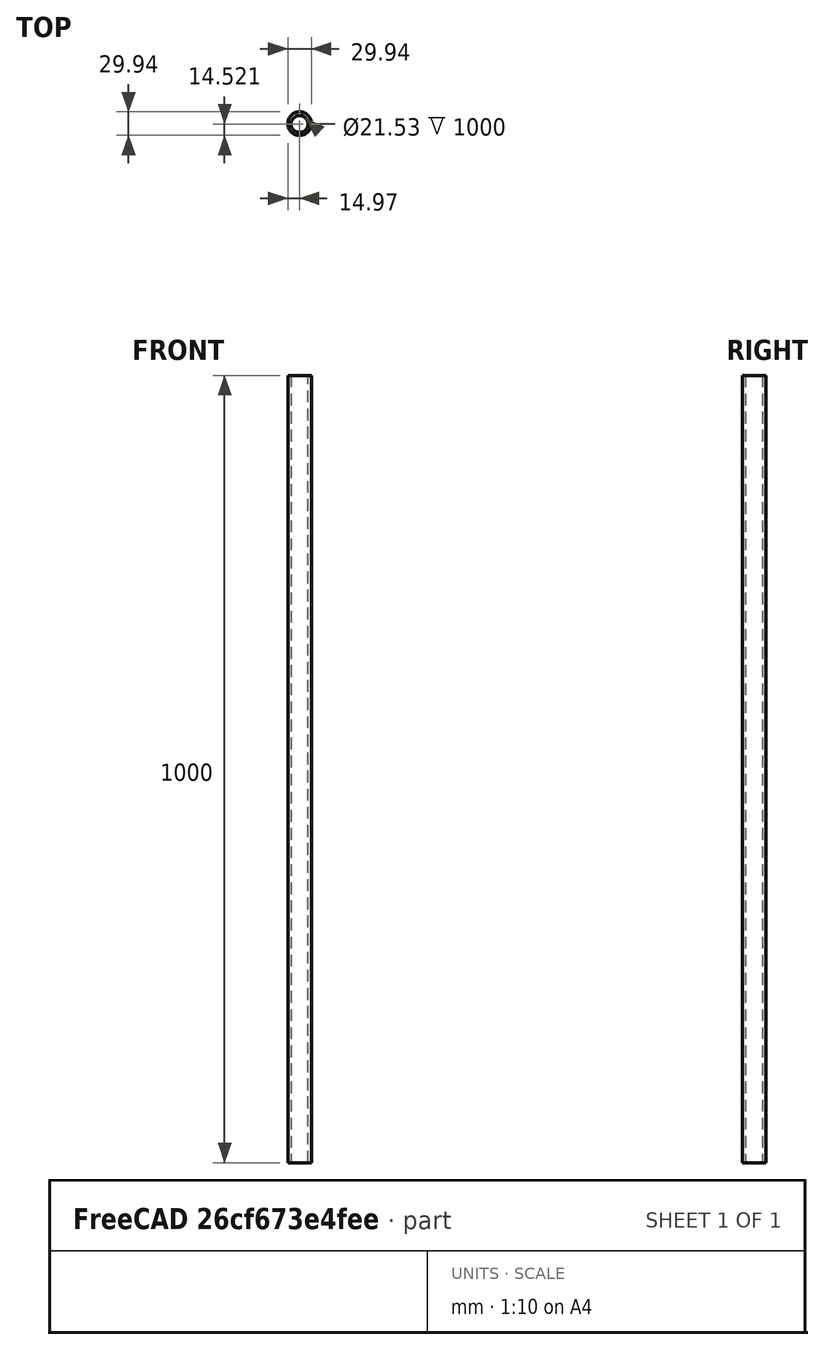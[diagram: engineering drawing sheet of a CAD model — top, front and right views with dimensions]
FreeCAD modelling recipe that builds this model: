
FCSTD DOCUMENT  (FreeCAD 1.1R20260723 (Git shallow))
Label: ALTube
License: All rights reserved
LicenseURL: https://en.wikipedia.org/wiki/All_rights_reserved
objects: App::Point×1, Sketcher::SketchObject×1, PartDesign::Pad×1, PartDesign::Body×1
note: 6 computed .brp shape members not serialized (recipe doc carries the construction recipe); baked Part::Feature solids carry a one-line shape summary decoded from their .brp

FEATURE [App::Point] Origin001
  Role = Origin
FEATURE [Sketcher::SketchObject] Sketch
  ArcFitTolerance = 1e-06
  AttachmentSupport = -> [Origin]
  ExternalTypes = [0]
  FullyConstrained = false
  MakeInternals = false
  MapMode = 5
  _ExternalGeoVersion = 1
  sketch-geometry (2):
    g0: Circle CenterX=0 CenterY=0 CenterZ=0 NormalX=0 NormalY=0 NormalZ=1 AngleXU=0 Radius=14.9679
    g1: Circle CenterX=0 CenterY=-0.449051 CenterZ=0 NormalX=0 NormalY=0 NormalZ=1 AngleXU=0 Radius=10.7661
  constraints (2):
    c: Coincident(g0,g-1)
    c: PointOnObject(g1,g-2)
FEATURE [PartDesign::Pad] Pad
  Direction = (0,0,1)
  FuzzyTolerance = -1
  Length = 1000
  Length2 = 10
  Profile = -> Sketch
  ReferenceAxis = -> Sketch [N_Axis]
  Refine = true
  SideType = 0
  Suppressed = false
  Type = 0
  Type2 = 0
FEATURE [PartDesign::Body] Body
  AllowCompound = true
  Group = -> [Sketch,Pad]
  Origin = -> Origin
  Tip = -> Pad
